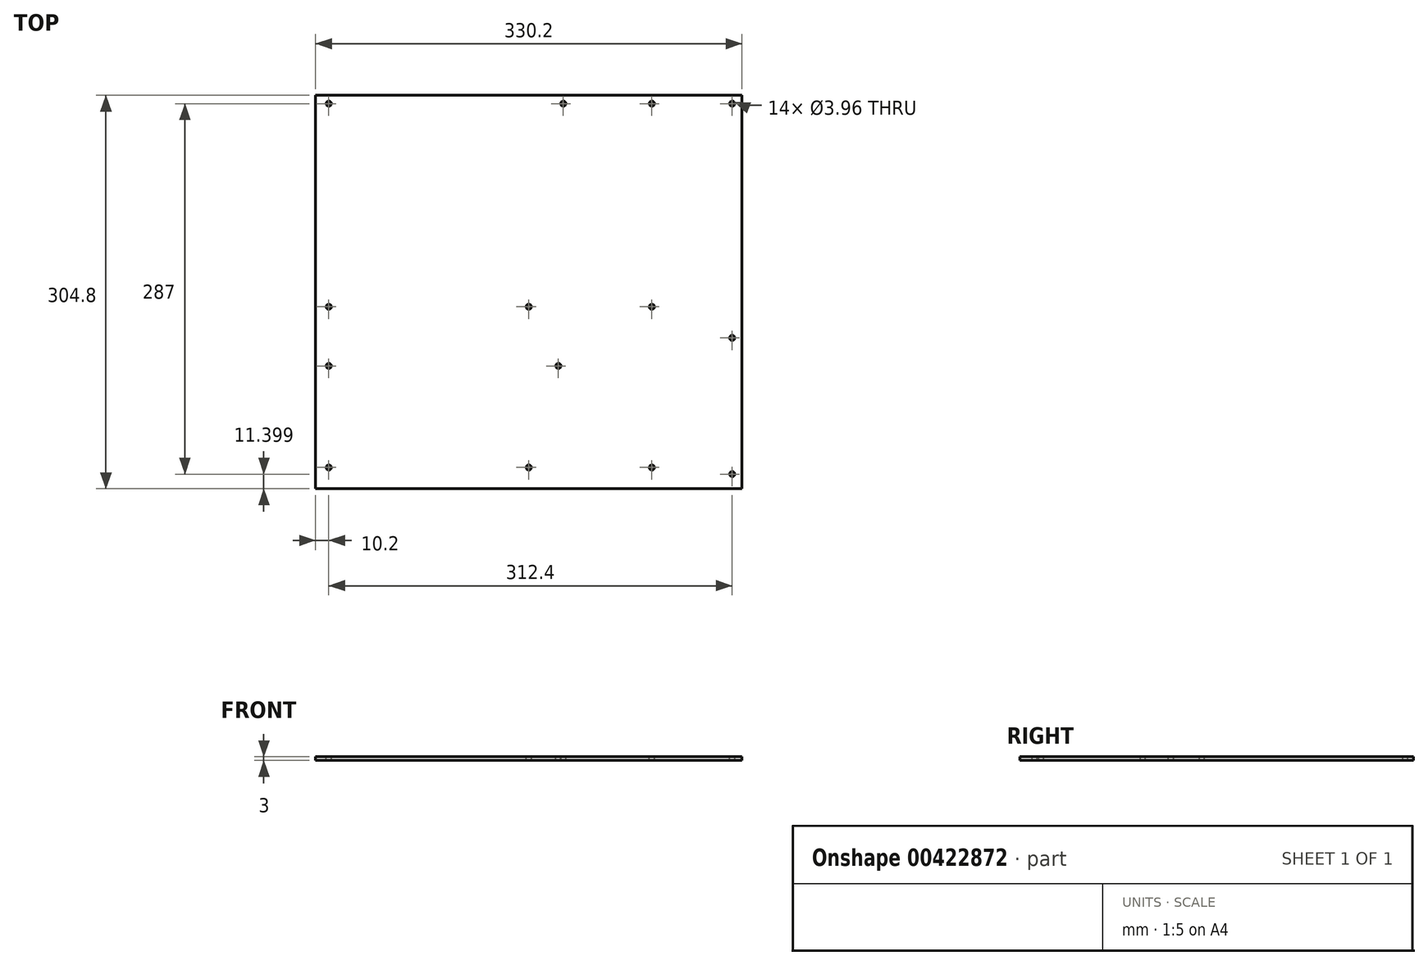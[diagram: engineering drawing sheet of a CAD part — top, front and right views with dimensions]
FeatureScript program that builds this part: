
annotation { "Feature Type Name" : "Feature", "Feature Type Description" : "" }
export const myFeature = defineFeature(function(context is Context, id is Id, definition is map)
    precondition{}
    {
        {
            var Q0;
            Q0=qCreatedBy(makeId("Top.planeOp"),FACE);
            var sketch = newSketch(context, id + "F0", { "sketchPlane" : qUnion([Q0])});
            skLineSegment(sketch, "E0.bottom", {"start": v(-165.1, 157.4) * mm, "end": v(165.1, 157.4) * mm});
            skLineSegment(sketch, "E0.top", {"start": v(-165.1, -147.4) * mm, "end": v(165.1, -147.4) * mm});
            skLineSegment(sketch, "E0.left", {"start": v(-165.1, 157.4) * mm, "end": v(-165.1, -147.4) * mm});
            skLineSegment(sketch, "E0.right", {"start": v(165.1, 157.4) * mm, "end": v(165.1, -147.4) * mm});
            skCircle(sketch, "E1", {"center": v(-154.9, -130.9) * mm, "radius": 1.98 * mm});
            skCircle(sketch, "E2", {"center": v(-154.9, -52.2) * mm, "radius": 1.98 * mm});
            skCircle(sketch, "E3", {"center": v(-154.9, 151) * mm, "radius": 1.98 * mm});
            skCircle(sketch, "E4", {"center": v(26.7, 151) * mm, "radius": 1.98 * mm});
            skCircle(sketch, "E5", {"center": v(95.3, 151) * mm, "radius": 1.98 * mm});
            skCircle(sketch, "E6", {"center": v(157.5, 151) * mm, "radius": 1.98 * mm});
            skCircle(sketch, "E7", {"center": v(95.3, -6.4) * mm, "radius": 1.98 * mm});
            skCircle(sketch, "E8", {"center": v(22.9, -52.2) * mm, "radius": 1.98 * mm});
            skCircle(sketch, "E9", {"center": v(157.5, -30.46) * mm, "radius": 1.98 * mm});
            skCircle(sketch, "E10", {"center": v(0, -130.9) * mm, "radius": 1.98 * mm});
            skCircle(sketch, "E11", {"center": v(95.3, -130.9) * mm, "radius": 1.98 * mm});
            skCircle(sketch, "E12", {"center": v(-154.9, -6.4) * mm, "radius": 1.98 * mm});
            skCircle(sketch, "E13", {"center": v(157.5, -136) * mm, "radius": 1.98 * mm});
            skCircle(sketch, "E14", {"center": v(0, -6.4) * mm, "radius": 1.98 * mm});
            skSolve(sketch);
        }
        {
            var Q0;
            Q0=makeQuery(id+"F0.imprint","IMPRINT",FACE,{"disambiguationData":[TD([[makeQuery(id+"F0.imprint","IMPRINT",EDGE,{"derivedFrom":sQuery(id+"F0.wireOp",EDGE,"E0.bottom")}),-1.0]])]});
            extrude(context, id + "F1", {"entities" : qUnion([Q0]), "oppositeDirection" : true, "depth" : 3 * mm});
        }
    });
